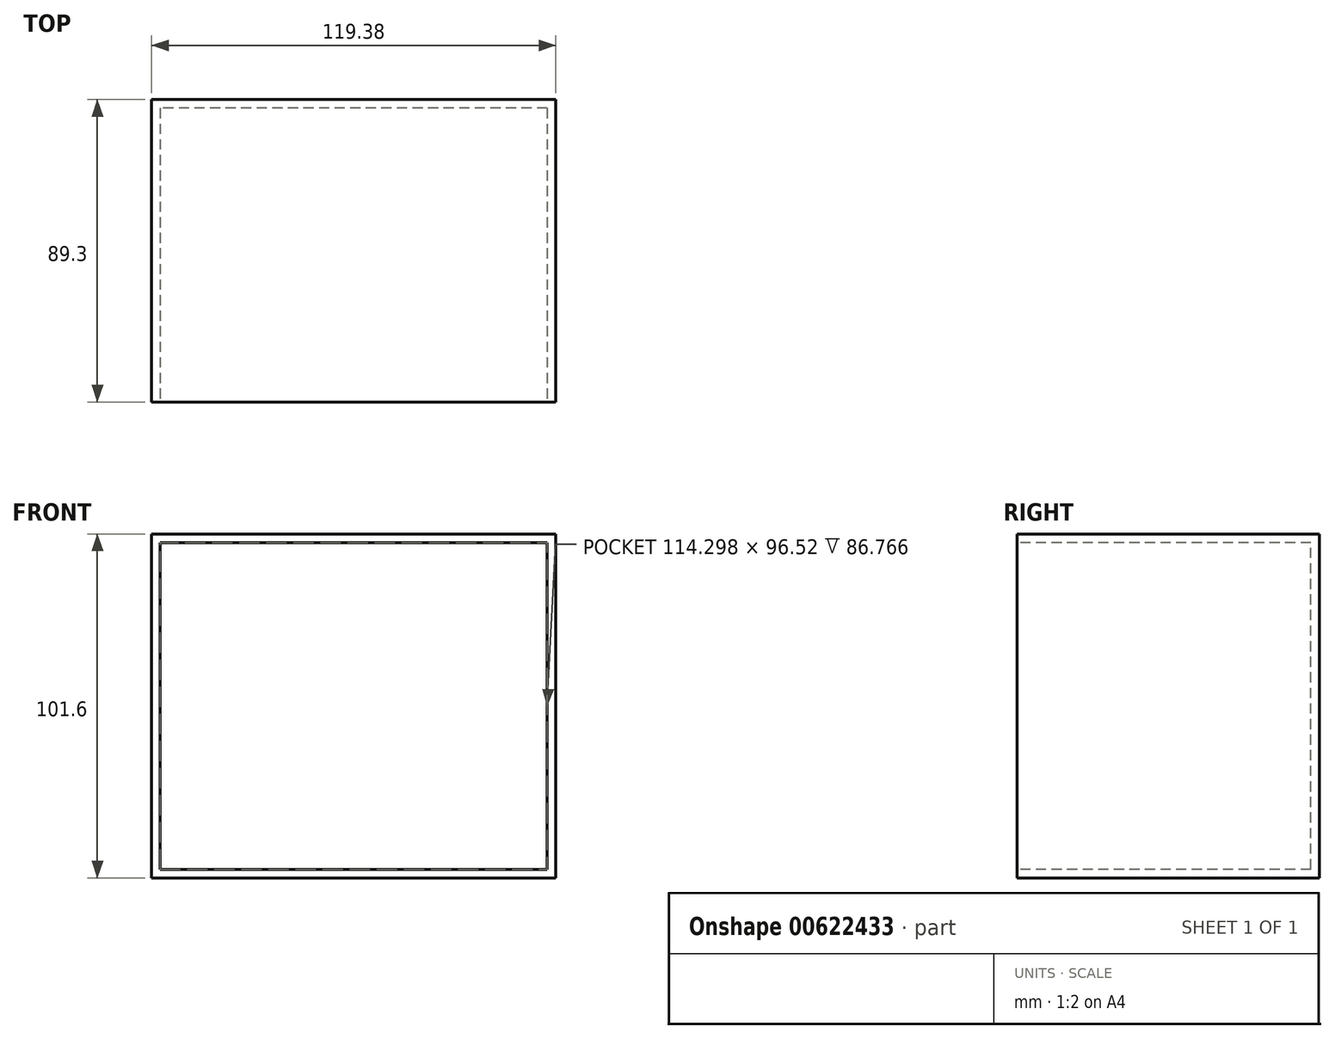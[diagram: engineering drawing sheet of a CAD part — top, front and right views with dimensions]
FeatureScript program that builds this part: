
annotation { "Feature Type Name" : "Feature", "Feature Type Description" : "" }
export const myFeature = defineFeature(function(context is Context, id is Id, definition is map)
    precondition{}
    {
        {
            var Q0;
            Q0=qCreatedBy(makeId("Top.planeOp"),FACE);
            var sketch = newSketch(context, id + "F0", { "sketchPlane" : qUnion([Q0])});
            skLineSegment(sketch, "E0.bottom", {"start": v(59.69, 44.65) * mm, "end": v(-59.69, 44.65) * mm});
            skLineSegment(sketch, "E0.top", {"start": v(59.69, -44.65) * mm, "end": v(-59.69, -44.65) * mm});
            skLineSegment(sketch, "E0.left", {"start": v(59.69, 44.65) * mm, "end": v(59.69, -44.65) * mm});
            skLineSegment(sketch, "E0.right", {"start": v(-59.69, 44.65) * mm, "end": v(-59.69, -44.65) * mm});
            skPoint(sketch, "E0.middle", {"position": v(0, 0) * mm});
            skSolve(sketch);
        }
        {
            var Q0;
            Q0=makeQuery(id+"F0.imprint","IMPRINT",FACE,{"disambiguationData":[TD([[makeQuery(id+"F0.imprint","IMPRINT",EDGE,{"derivedFrom":sQuery(id+"F0.wireOp",EDGE,"E0.bottom")}),1.0]])]});
            extrude(context, id + "F1", {"entities" : qUnion([Q0]), "oppositeDirection" : true, "depth" : 50.8 * mm, "offsetDistance" : 25.4 * mm, "hasSecondDirection" : true, "secondDirectionOppositeDirection" : false, "secondDirectionDepth" : 50.8 * mm});
        }
        {
            var Q0;
            Q0=makeQuery(id+"F1.opExtrude","SWEPT_FACE",FACE,{"disambiguationData":[OSD([sQuery(id+"F0.wireOp",EDGE,"E0.top")])]});
            shell(context, id + "F2", {"entities" : qUnion([Q0]), "thickness" : 2.54 * mm});
        }
    });
